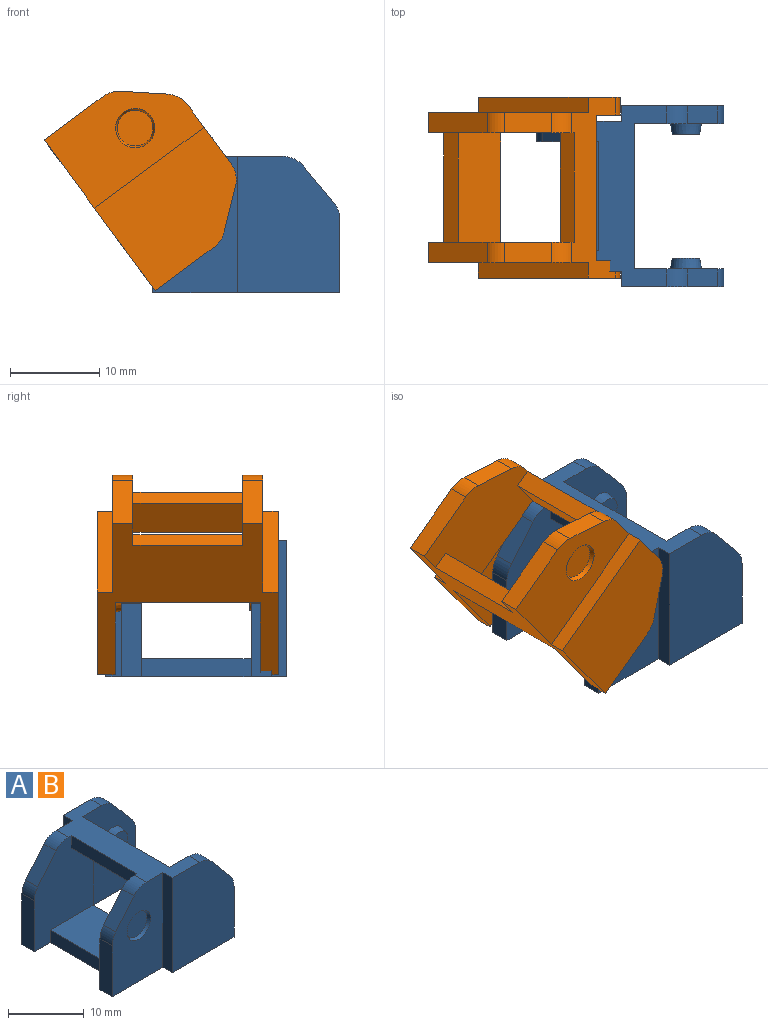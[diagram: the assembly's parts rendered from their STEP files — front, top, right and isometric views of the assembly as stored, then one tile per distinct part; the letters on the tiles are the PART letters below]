
ASSEMBLY  parts=2 mates=1
PART A: 41 faces, bbox 21x20.3x15.3 mm
  f0: plane 15.3x11mm, normal (0,-1,0), area 128.7mm2, adj f2,f14,f15,f16,f17,f18,f19,f24
  f1: plane 15.3x11mm, normal (0,1,0), area 128.7mm2, adj f2,f3,f15,f16,f17,f18,f19,f24
  f2: plane 16.3x15.3mm, normal (1,0,0), area 110.4mm2, adj f0,f1,f8,f9,f15,f16,f18,f19
  f3: plane 8.21x2.25mm, normal (-1,0,0), area 18.5mm2, adj f1,f4,f16,f29
  f4: plane 15.3x9.5mm, normal (0,-1,0), area 114.7mm2, adj f3,f5,f15,f16,f28,f29,f35,f37
  f5: plane 15.3x1.75mm, normal (-1,0,0), area 26.8mm2, adj f4,f6,f15,f16
  f6: plane 15.3x11.5mm, normal (0,-1,0), area 160.5mm2, adj f5,f7,f15,f16,f25,f32,f36
  f7: plane 8.21x2mm, normal (1,0,0), area 16.4mm2, adj f6,f8,f16,f36
  f8: plane 15.3x10mm, normal (0,1,0), area 128mm2, adj f2,f7,f15,f16,f25,f32,f36,f39
  f9: plane 15.3x10mm, normal (0,-1,0), area 128mm2, adj f2,f10,f15,f16,f26,f31,f33,f38
  f10: plane 8.21x2mm, normal (1,0,0), area 16.4mm2, adj f9,f11,f16,f31
  f11: plane 15.3x11.5mm, normal (0,1,0), area 160.5mm2, adj f10,f12,f15,f16,f26,f31,f33
  f12: plane 15.3x1.75mm, normal (-1,0,0), area 26.8mm2, adj f11,f13,f15,f16
  f13: plane 15.3x9.5mm, normal (0,1,0), area 114.7mm2, adj f12,f14,f15,f16,f27,f30,f34,f40
  f14: plane 8.21x2.25mm, normal (-1,0,0), area 18.5mm2, adj f0,f13,f16,f30
  f15: plane 20.3x8.19mm, normal (0,0,1), area 90.7mm2, adj f0,f1,f2,f4,f5,f6,f8,f9
  f16: plane 21x20.3mm, normal (0,0,-1), area 193.1mm2, adj f0,f1,f2,f3,f4,f5,f6,f7
  f17: plane 12.3x2mm, normal (-1,0,0), area 24.6mm2, adj f0,f1,f16,f18
  f18: plane 12.3x8mm, normal (0,0,1), area 98.4mm2, adj f0,f1,f2,f17
  f19: plane 12.3x4.1mm, normal (0,0,-1), area 50.4mm2, adj f0,f1,f2,f24
  f20: plane 3.1x3.1mm, normal (0,1,0), area 7.5mm2, adj f39
  f21: plane 3.1x3.1mm, normal (0,-1,0), area 7.5mm2, adj f38
  f22: plane 4x4mm, normal (0,-1,0), area 12.6mm2, adj f37
  f23: plane 4x4mm, normal (0,1,0), area 12.6mm2, adj f40
  f24: plane 12.3x2mm, normal (-1,0,0), area 24.6mm2, adj f0,f1,f15,f19
  f25: plane 4.09x3.41mm, normal (0.77,0,0.64), area 10.6mm2, adj f6,f8,f32,f36
  f26: plane 4.09x3.41mm, normal (0.77,0,0.64), area 10.6mm2, adj f9,f11,f31,f33
  f27: plane 4.09x3.41mm, normal (-0.77,0,0.64), area 12mm2, adj f0,f13,f30,f34
  f28: plane 4.09x3.41mm, normal (-0.77,0,0.64), area 12mm2, adj f1,f4,f29,f35
  f29: cylinder r=3mm len=2.25mm, axis (0,-1,0), area 4.7mm2, adj f1,f3,f4,f28
  f30: cylinder r=3mm len=2.25mm, axis (0,-1,0), area 4.7mm2, adj f0,f13,f14,f27
  f31: cylinder r=3mm len=2mm, axis (0,1,0), area 4.2mm2, adj f9,f10,f11,f26
  f32: cylinder r=3mm len=2.3mm, axis (0,-1,0), area 5.3mm2, adj f6,f8,f15,f25
  f33: cylinder r=3mm len=2.3mm, axis (0,-1,0), area 5.3mm2, adj f9,f11,f15,f26
  f34: cylinder r=3mm len=2.3mm, axis (0,-1,0), area 5.9mm2, adj f0,f13,f15,f27
  f35: cylinder r=3mm len=2.3mm, axis (0,-1,0), area 5.9mm2, adj f1,f4,f15,f28
  f36: cylinder r=3mm len=2mm, axis (0,1,0), area 4.2mm2, adj f6,f7,f8,f25
  f37: cone r=2mm half-angle=21.8deg, axis (0,-1,0), area 7.1mm2, adj f4,f22
  f38: cone r=1.75mm half-angle=9.5deg, axis (0,1,0), area 12.6mm2, adj f9,f21
  f39: cone r=1.55mm half-angle=9.5deg, axis (0,-1,0), area 12.6mm2, adj f8,f20
  f40: cone r=2.2mm half-angle=21.8deg, axis (0,1,0), area 7.1mm2, adj f13,f23
PART B: same geometry as A
PLACE A t=(-9.85,6.43,4.04)mm
PLACE B rot(axis=(0,1,0),53.6deg) t=(-28.23,7.38,8.91)mm
MATE revolute B.f38 <-> A.f37  axis (0,-1,0) through (-20.1,14.33,13.04)mm
